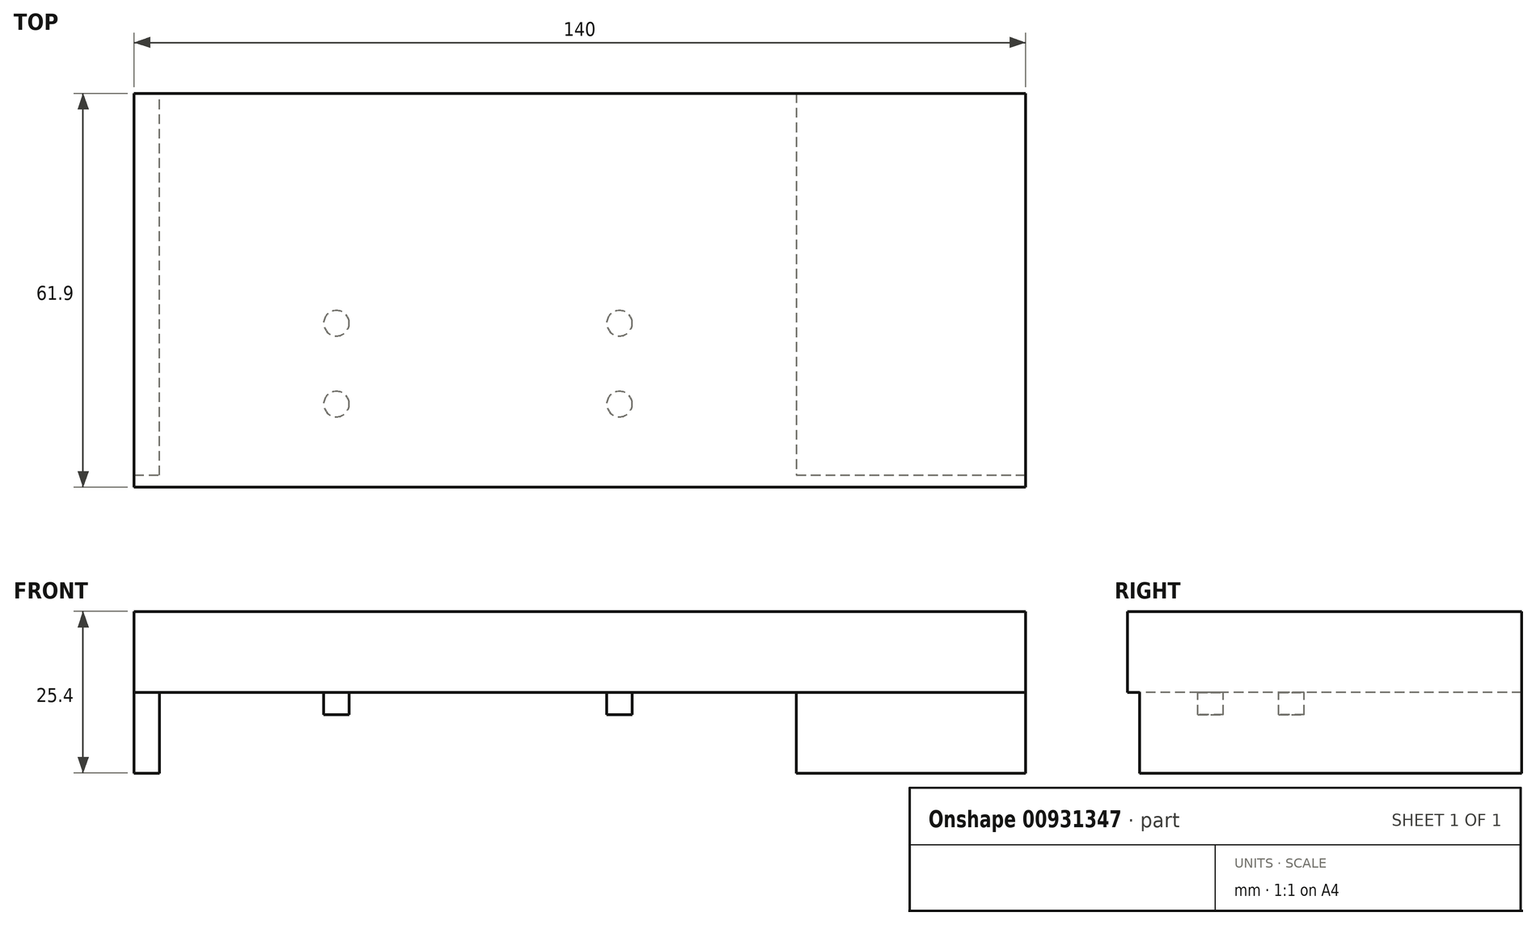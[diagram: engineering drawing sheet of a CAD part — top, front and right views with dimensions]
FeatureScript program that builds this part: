
annotation { "Feature Type Name" : "Feature", "Feature Type Description" : "" }
export const myFeature = defineFeature(function(context is Context, id is Id, definition is map)
    precondition{}
    {
        {
            var Q0;
            Q0=qCreatedBy(makeId("Front.planeOp"),FACE);
            var sketch = newSketch(context, id + "F0", { "sketchPlane" : qUnion([Q0])});
            skLineSegment(sketch, "E0.bottom", {"start": v(-59.2, -7.6) * mm, "end": v(80.8, -7.6) * mm});
            skLineSegment(sketch, "E0.top", {"start": v(-59.2, -33) * mm, "end": v(80.8, -33) * mm});
            skLineSegment(sketch, "E0.left", {"start": v(-59.2, -7.6) * mm, "end": v(-59.2, -33) * mm});
            skLineSegment(sketch, "E0.right", {"start": v(80.8, -7.6) * mm, "end": v(80.8, -33) * mm});
            skSolve(sketch);
        }
        {
            var Q0;
            Q0 = qSketchRegion(id + "F0", true);
            extrude(context, id + "F1", {"entities" : qUnion([Q0]), "depth" : 61.9 * mm, "offsetDistance" : 25.4 * mm});
        }
        {
            var Q0;
            Q0=makeQuery(id+"F1.opExtrude","SWEPT_FACE",FACE,{"disambiguationData":[OSD([sQuery(id+"F0.wireOp",EDGE,"E0.top")])]});
            var sketch = newSketch(context, id + "F2", { "sketchPlane" : qUnion([Q0])});
            skLineSegment(sketch, "E1", {"start": v(44.8, 0) * mm, "end": v(44.8, 60) * mm});
            skLineSegment(sketch, "E2", {"start": v(44.8, 60) * mm, "end": v(80.8, 60) * mm});
            skLineSegment(sketch, "E3", {"start": v(80.8, 60) * mm, "end": v(80.8, 61.9) * mm});
            skLineSegment(sketch, "E4", {"start": v(80.8, 61.9) * mm, "end": v(-59.2, 61.9) * mm});
            skLineSegment(sketch, "E5", {"start": v(-59.2, 61.9) * mm, "end": v(-59.2, 60) * mm});
            skLineSegment(sketch, "E6", {"start": v(-59.2, 60) * mm, "end": v(-55.2, 60) * mm});
            skLineSegment(sketch, "E7", {"start": v(-55.2, 60) * mm, "end": v(-55.2, 0) * mm});
            skLineSegment(sketch, "E8", {"start": v(-55.2, 0) * mm, "end": v(44.8, 0) * mm});
            skSolve(sketch);
        }
        {
            var Q0;
            Q0 = qSketchRegion(id + "F2", true);
            extrude(context, id + "F3", {"entities" : qUnion([Q0]), "operationType" : NewBodyOperationType.REMOVE, "oppositeDirection" : true, "depth" : 12.7 * mm, "offsetDistance" : 25.4 * mm});
        }
        {
            var Q0;
            Q0=makeQuery(id+"F3.boolean.opBoolean","COPY",FACE,{"derivedFrom":makeQuery(id+"F3.opExtrude","CAP_FACE",FACE,{"disambiguationData":[OSD([sQuery(id+"F2.wireOp",EDGE,"E1"),sQuery(id+"F2.wireOp",EDGE,"E2"),sQuery(id+"F2.wireOp",EDGE,"E3"),sQuery(id+"F2.wireOp",EDGE,"E4"),sQuery(id+"F2.wireOp",EDGE,"E5"),sQuery(id+"F2.wireOp",EDGE,"E6"),sQuery(id+"F2.wireOp",EDGE,"E7"),sQuery(id+"F2.wireOp",EDGE,"E8")])],"isStart":false})});
            var sketch = newSketch(context, id + "F4", { "sketchPlane" : qUnion([Q0])});
            skCircle(sketch, "E9", {"center": v(-27.43, 48.82) * mm, "radius": 2 * mm});
            skCircle(sketch, "E10", {"center": v(-27.43, 36.12) * mm, "radius": 2 * mm});
            skCircle(sketch, "E11", {"center": v(17.02, 48.82) * mm, "radius": 2 * mm});
            skCircle(sketch, "E12", {"center": v(17.02, 36.12) * mm, "radius": 2 * mm});
            skSolve(sketch);
        }
        {
            var Q0;
            Q0 = qSketchRegion(id + "F4", true);
            extrude(context, id + "F5", {"entities" : qUnion([Q0]), "operationType" : NewBodyOperationType.ADD, "depth" : 3.5 * mm, "offsetDistance" : 25.4 * mm});
        }
    });
